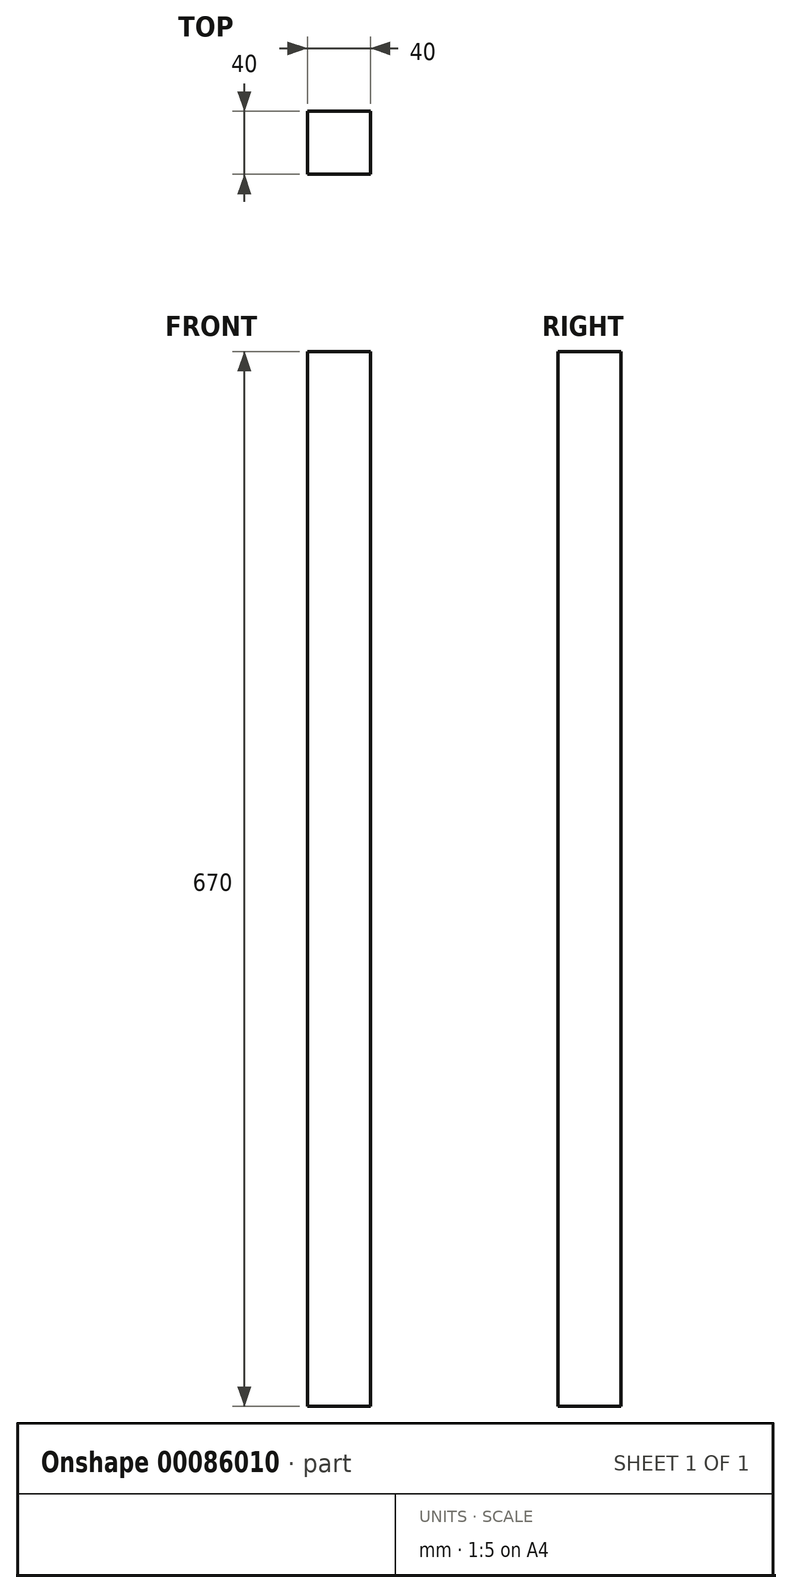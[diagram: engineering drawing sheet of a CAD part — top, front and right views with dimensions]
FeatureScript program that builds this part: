
annotation { "Feature Type Name" : "Feature", "Feature Type Description" : "" }
export const myFeature = defineFeature(function(context is Context, id is Id, definition is map)
    precondition{}
    {
        {
            var Q0;
            Q0=qCreatedBy(makeId("Top.planeOp"),FACE);
            var sketch = newSketch(context, id + "F0", { "sketchPlane" : qUnion([Q0])});
            skLineSegment(sketch, "E0.bottom", {"start": v(20, 20) * mm, "end": v(-20, 20) * mm});
            skLineSegment(sketch, "E0.top", {"start": v(20, -20) * mm, "end": v(-20, -20) * mm});
            skLineSegment(sketch, "E0.left", {"start": v(20, 20) * mm, "end": v(20, -20) * mm});
            skLineSegment(sketch, "E0.right", {"start": v(-20, 20) * mm, "end": v(-20, -20) * mm});
            skPoint(sketch, "E0.middle", {"position": v(0, 0) * mm});
            skSolve(sketch);
        }
        {
            var Q0;
            Q0=makeQuery(id+"F0.imprint","IMPRINT",FACE,{"disambiguationData":[TD([[makeQuery(id+"F0.imprint","IMPRINT",EDGE,{"derivedFrom":sQuery(id+"F0.wireOp",EDGE,"E0.bottom")}),1.0]])]});
            extrude(context, id + "F1", {"entities" : qUnion([Q0]), "depth" : 670 * mm});
        }
    });
